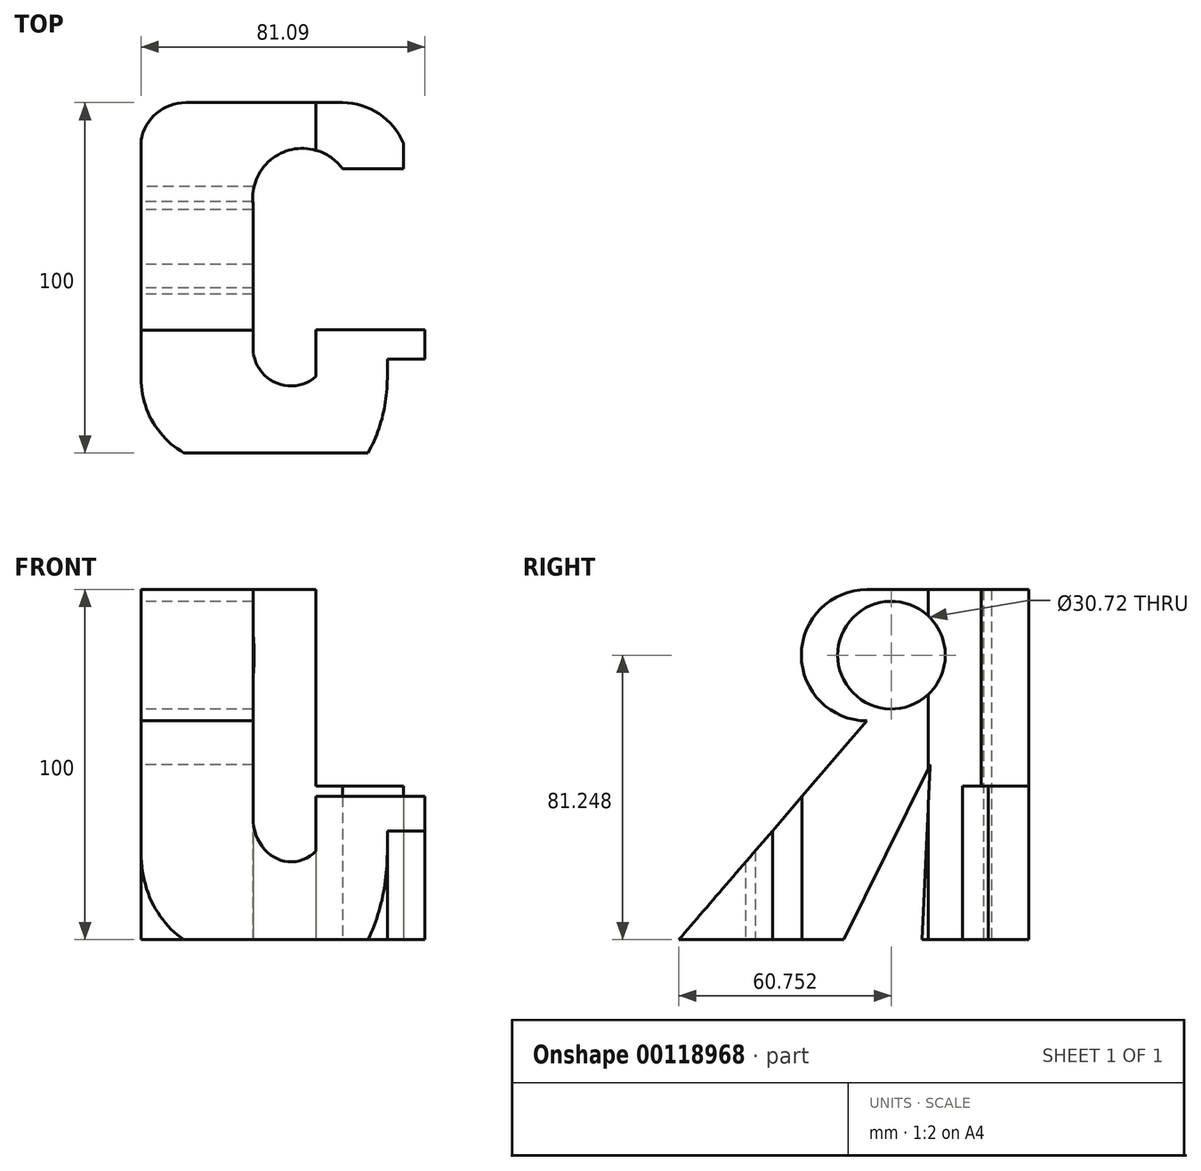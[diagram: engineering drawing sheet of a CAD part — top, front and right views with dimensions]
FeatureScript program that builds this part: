
annotation { "Feature Type Name" : "Feature", "Feature Type Description" : "" }
export const myFeature = defineFeature(function(context is Context, id is Id, definition is map)
    precondition{}
    {
        {
            var Q0;
            Q0=qCreatedBy(makeId("Top.planeOp"),FACE);
            var sketch = newSketch(context, id + "F0", { "sketchPlane" : qUnion([Q0])});
            skLineSegment(sketch, "E0.bottom", {"start": v(50, -50) * mm, "end": v(-50, -50) * mm, "construction": true});
            skLineSegment(sketch, "E0.top", {"start": v(50, 50) * mm, "end": v(-50, 50) * mm, "construction": true});
            skLineSegment(sketch, "E0.left", {"start": v(50, -50) * mm, "end": v(50, 50) * mm, "construction": true});
            skLineSegment(sketch, "E0.right", {"start": v(-50, -50) * mm, "end": v(-50, 50) * mm, "construction": true});
            skPoint(sketch, "E0.middle", {"position": v(0, 0) * mm});
            skLineSegment(sketch, "E1", {"start": v(-37.2, 50) * mm, "end": v(7.56, 50) * mm});
            skArc(sketch, "E2", {"start": v(-37.2, 50) * mm, "mid": v(-45.56, 46.95) * mm, "end": v(-50, 39.23) * mm});
            skLineSegment(sketch, "E3", {"start": v(-50, 39.23) * mm, "end": v(-50, -28.77) * mm});
            skArc(sketch, "E4", {"start": v(-50, -28.77) * mm, "mid": v(-46.73, -41.02) * mm, "end": v(-37.78, -50) * mm});
            skArc(sketch, "E5", {"start": v(25, 38.36) * mm, "mid": v(18.04, 46.82) * mm, "end": v(7.56, 50) * mm});
            skLineSegment(sketch, "E6", {"start": v(25, 38.36) * mm, "end": v(25, 31.1) * mm});
            skLineSegment(sketch, "E7", {"start": v(25, 31.1) * mm, "end": v(7.56, 31.12) * mm});
            skArc(sketch, "E8", {"start": v(7.56, 31.12) * mm, "mid": v(-9.04, 36) * mm, "end": v(-18.02, 21.21) * mm});
            skLineSegment(sketch, "E9", {"start": v(-18.02, 21.21) * mm, "end": v(-18.02, -20.05) * mm});
            skLineSegment(sketch, "E10", {"start": v(-37.78, -50) * mm, "end": v(14.82, -50) * mm});
            skArc(sketch, "E11", {"start": v(-18.02, -20.05) * mm, "mid": v(-11.63, -29.94) * mm, "end": v(0, -28.19) * mm});
            skLineSegment(sketch, "E12", {"start": v(0, -28.19) * mm, "end": v(0, -14.82) * mm});
            skLineSegment(sketch, "E13", {"start": v(0, -14.82) * mm, "end": v(31.1, -14.82) * mm});
            skLineSegment(sketch, "E14", {"start": v(31.1, -14.82) * mm, "end": v(31.1, -23.25) * mm});
            skLineSegment(sketch, "E15", {"start": v(31.1, -23.25) * mm, "end": v(20.34, -23.25) * mm});
            skLineSegment(sketch, "E16", {"start": v(20.34, -23.25) * mm, "end": v(20.34, -28.77) * mm});
            skArc(sketch, "E17", {"start": v(14.82, -50) * mm, "mid": v(18.94, -39.74) * mm, "end": v(20.34, -28.77) * mm});
            skSolve(sketch);
        }
        {
            var Q0;
            Q0=qCreatedBy(makeId("Right.planeOp"),FACE);
            var sketch = newSketch(context, id + "F1", { "sketchPlane" : qUnion([Q0])});
            skPoint(sketch, "E18.middle", {"position": v(0, 0) * mm});
            skLineSegment(sketch, "E19.bottom", {"start": v(-50, 50) * mm, "end": v(50, 50) * mm, "construction": true});
            skLineSegment(sketch, "E19.top", {"start": v(-50, -50) * mm, "end": v(50, -50) * mm, "construction": true});
            skLineSegment(sketch, "E19.left", {"start": v(-50, 50) * mm, "end": v(-50, -50) * mm, "construction": true});
            skLineSegment(sketch, "E19.right", {"start": v(50, 50) * mm, "end": v(50, -50) * mm, "construction": true});
            skLineSegment(sketch, "E20", {"start": v(-50, 50) * mm, "end": v(-50, -50) * mm});
            skLineSegment(sketch, "E21", {"start": v(-50, 50) * mm, "end": v(-23.54, 50) * mm});
            skLineSegment(sketch, "E22", {"start": v(19.47, -50) * mm, "end": v(0, -50) * mm});
            skLineSegment(sketch, "E23", {"start": v(-22.08, -50) * mm, "end": v(-50, -50) * mm});
            skLineSegment(sketch, "E24", {"start": v(50, 50) * mm, "end": v(50, -50) * mm});
            skLineSegment(sketch, "E25", {"start": v(50, 50) * mm, "end": v(3.78, 50) * mm});
            skArc(sketch, "E26", {"start": v(3.78, 50) * mm, "mid": v(-14.97, 31.25) * mm, "end": v(3.78, 12.5) * mm});
            skLineSegment(sketch, "E27", {"start": v(-28.19, -50) * mm, "end": v(-8.43, -50) * mm});
            skLineSegment(sketch, "E28", {"start": v(-8.43, -50) * mm, "end": v(-2.9, -50) * mm});
            skLineSegment(sketch, "E29", {"start": v(-2.9, -50) * mm, "end": v(21.8, 0) * mm});
            skLineSegment(sketch, "E30", {"start": v(21.8, 0) * mm, "end": v(19.47, -50) * mm});
            skLineSegment(sketch, "E31", {"start": v(50, -50) * mm, "end": v(19.47, -50) * mm});
            skCircle(sketch, "E32", {"center": v(10.75, 31.25) * mm, "radius": 15.36 * mm});
            skLineSegment(sketch, "E33", {"start": v(3.78, 12.5) * mm, "end": v(-50, -50) * mm});
            skSolve(sketch);
        }
        {
            var Q0;
            Q0=qCreatedBy(makeId("Front.planeOp"),FACE);
            var sketch = newSketch(context, id + "F2", { "sketchPlane" : qUnion([Q0])});
            skPoint(sketch, "E34.middle", {"position": v(0, 0) * mm});
            skLineSegment(sketch, "E35.bottom", {"start": v(50, -50) * mm, "end": v(-50, -50) * mm, "construction": true});
            skLineSegment(sketch, "E35.top", {"start": v(50, 50) * mm, "end": v(-50, 50) * mm, "construction": true});
            skLineSegment(sketch, "E35.left", {"start": v(50, -50) * mm, "end": v(50, 50) * mm, "construction": true});
            skLineSegment(sketch, "E35.right", {"start": v(-50, -50) * mm, "end": v(-50, 50) * mm, "construction": true});
            skLineSegment(sketch, "E36", {"start": v(-50, 50) * mm, "end": v(0, 50) * mm});
            skLineSegment(sketch, "E37", {"start": v(0, 50) * mm, "end": v(0, -6.1) * mm});
            skLineSegment(sketch, "E38", {"start": v(0, -6.1) * mm, "end": v(50, -6.1) * mm});
            skLineSegment(sketch, "E39", {"start": v(50, -6.1) * mm, "end": v(50, -50) * mm});
            skLineSegment(sketch, "E40", {"start": v(-50, -50) * mm, "end": v(-50, 50) * mm});
            skLineSegment(sketch, "E41", {"start": v(50, -50) * mm, "end": v(-50, -50) * mm});
            skSolve(sketch);
        }
        {
            var Q0;
            Q0 = qSketchRegion(id + "F2", true);
            extrude(context, id + "F3", {"entities" : qUnion([Q0]), "endBound" : BoundingType.SYMMETRIC, "depth" : 100 * mm});
        }
        {
            var Q0;
            Q0 = qSketchRegion(id + "F1", true);
            var Q1;
            Q1 = qConstructionFilter(qBodyType(qCreatedBy(id + "F1" ,EDGE), BodyType.WIRE), ConstructionObject.NO);
            extrude(context, id + "F4", {"entities" : qUnion([Q0]), "operationType" : NewBodyOperationType.INTERSECT, "surfaceEntities" : qUnion([Q1]), "endBound" : BoundingType.SYMMETRIC, "depth" : 100 * mm});
        }
        {
            var Q0;
            Q0 = qSketchRegion(id + "F0", true);
            extrude(context, id + "F5", {"entities" : qUnion([Q0]), "operationType" : NewBodyOperationType.INTERSECT, "endBound" : BoundingType.SYMMETRIC, "depth" : 100 * mm});
        }
    });
